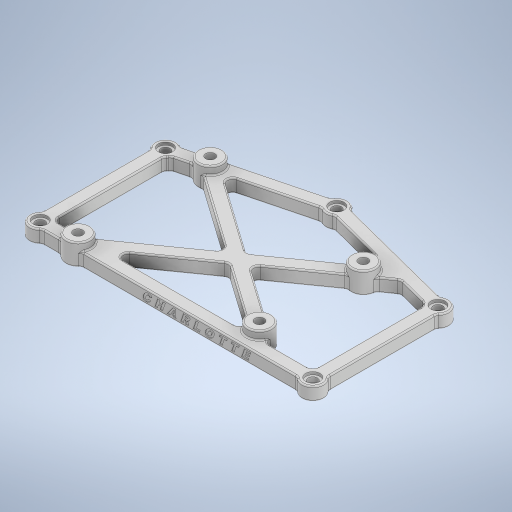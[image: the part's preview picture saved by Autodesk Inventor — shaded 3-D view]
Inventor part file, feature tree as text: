
AUTODESK INVENTOR PART (.ipt)
format: ipt  version: 2024.2 (Build 282272000, 272)  size: 1,375,744 bytes
history: native  units: mm
features: sketch x8, extrude x7, emboss x3, fillet x2, hole x1
ambient origin geometry x8: Origin, YZ Plane, XZ Plane, XY Plane, X Axis, Y Axis, Z Axis, Center Point
bodies: Solid1 (feature_tree)
feature tree (21):
  sketch  "Sketch1"  dims[d0=4.9mm d1=101.0mm]
  extrude  "Extrusion1"  Depth=4.9mm
  extrude  "Extrusion2"  Depth=50.5mm
  extrude  "Extrusion3"  Depth=8.0mm
  hole  "Hole1"  [1 undecoded]
  extrude  "Extrusion4"  Depth=62.0mm
  extrude  "Extrusion5"  Depth=5.0mm
  fillet  "Fillet1"  Radius=2.5mm
  fillet  "Fillet3"  Radius=5.0mm
  emboss  "Emboss1"
  emboss  "Emboss4"
  emboss  "Emboss5"
  extrude  "Extrusion6"  Depth=2.5mm
  extrude  "Extrusion7"  Depth=2.5mm
  sketch  "Sketch3"  dims[d2=13.0mm d3=50.5mm]
  sketch  "Sketch4"  dims[d4=8.0mm d6=49.0mm]
  sketch  "Sketch5"  dims[d7=46.4mm d8=5.25mm]
  sketch  "Sketch8"  dims[d9=5.25mm d10=62.0mm]
  sketch  "Sketch9"  dims[d12=9.0mm d13=5.0mm d14=2.5mm d21=5.0mm]
  sketch  "Sketch10"  dims[d22=2.5mm d23=2.5mm]
  sketch  "Sketch11"  dims[d30=5.0mm d31=2.5mm d32=2.5mm d33=5.0mm d35=2.5mm d38=3.4mm d39=5.0mm d40=2.5mm d41=2.5mm d42=5.0mm d43=5.0mm d44=2.5mm d45=2.5mm d46=2.5mm d47=2.5mm d48=5.0mm d49=0.0mm d52=8.0mm d53=0.0mm d54=1.9mm d55=0.0mm d56=3.4mm d57=6.0mm d58=4.0mm d59=2.0mm d60=90.0deg d61=8.0mm d62=20.594885mm d63=5.7mm d64=5.0mm d65=0.0mm d66=5.25mm d67=1.0mm d68=0.0mm d69=2.0mm d71=25.0mm d75=0.25mm d76=0.0mm d81=0.2mm d82=0.0mm d83=0.2mm d84=0.0mm d85=0.5mm d86=0.25mm d87=0.0mm d88=0.25mm d89=0.0mm]
note: 1 required parameter value undecoded (feature->parameter linkage not recoverable at this tier; creation-order binding heuristic only, values carry confidence <= 0.55)
